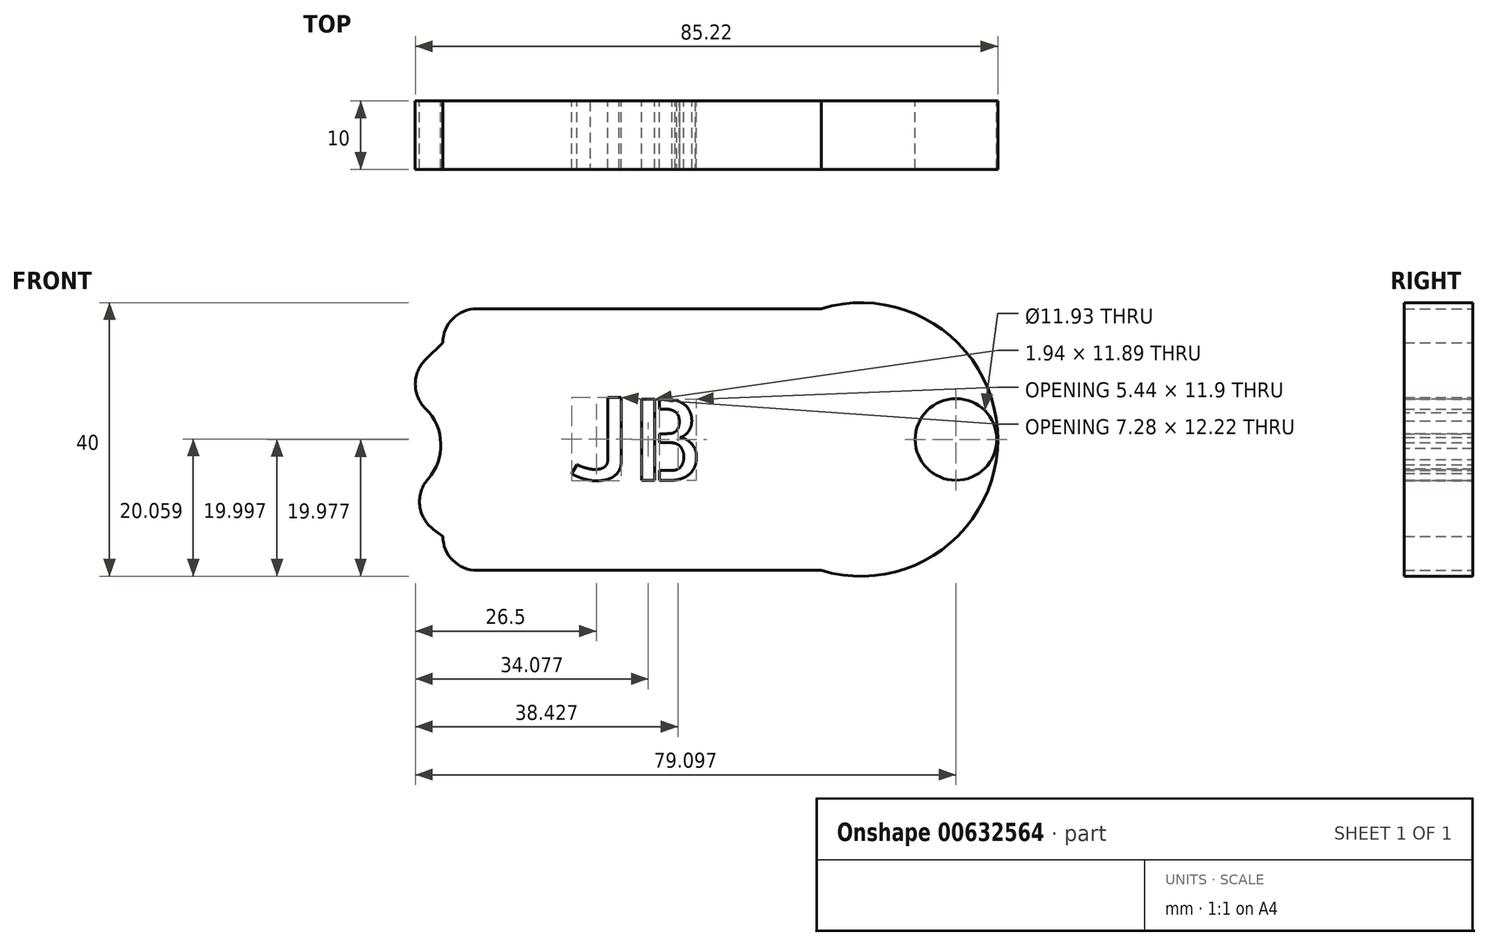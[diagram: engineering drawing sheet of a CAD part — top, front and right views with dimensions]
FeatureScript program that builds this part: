
annotation { "Feature Type Name" : "Feature", "Feature Type Description" : "" }
export const myFeature = defineFeature(function(context is Context, id is Id, definition is map)
    precondition{}
    {
        {
            var Q0;
            Q0=qCreatedBy(makeId("Front.planeOp"),FACE);
            var sketch = newSketch(context, id + "F0", { "sketchPlane" : qUnion([Q0])});
            skLineSegment(sketch, "E0.bottom", {"start": v(0, 0) * mm, "end": v(-50.38, 0) * mm});
            skLineSegment(sketch, "E0.top", {"start": v(0, 38.27) * mm, "end": v(-50.38, 38.27) * mm});
            skLineSegment(sketch, "E0.left", {"start": v(0, 0) * mm, "end": v(0, 38.27) * mm});
            skLineSegment(sketch, "E0.right", {"start": v(-55.38, 5) * mm, "end": v(-55.38, 33.27) * mm});
            skArc(sketch, "E1", {"start": v(0, 0) * mm, "mid": v(25.81, 19.14) * mm, "end": v(0, 38.27) * mm});
            skPoint(sketch, "E2.visualSharp", {"position": v(-55.38, 38.27) * mm});
            skArc(sketch, "E2.filletArc", {"start": v(-50.38, 38.27) * mm, "mid": v(-53.92, 36.8) * mm, "end": v(-55.38, 33.27) * mm});
            skPoint(sketch, "E3.visualSharp", {"position": v(-55.38, 0) * mm});
            skArc(sketch, "E3.filletArc", {"start": v(-55.38, 5) * mm, "mid": v(-53.92, 1.46) * mm, "end": v(-50.38, 0) * mm});
            skLineSegment(sketch, "E4", {"start": v(-55.38, 33.27) * mm, "end": v(-57.9, 30.8) * mm});
            skLineSegment(sketch, "E5", {"start": v(-55.38, 5) * mm, "end": v(-56.75, 6) * mm});
            skArc(sketch, "E6", {"start": v(-57.55, 13.35) * mm, "mid": v(-55.67, 18.58) * mm, "end": v(-57.92, 23.66) * mm});
            skLineSegment(sketch, "E7", {"start": v(-63.31, 10.8) * mm, "end": v(-63.31, 18.3) * mm});
            skText(sketch, "E8", { "text": "JB", "fontName": "AllertaStencil-Regular.ttf"});
            skPoint(sketch, "E9.visualSharp", {"position": v(-63.03, 25.8) * mm});
            skArc(sketch, "E9.filletArc", {"start": v(-57.9, 30.8) * mm, "mid": v(-59.41, 27.24) * mm, "end": v(-57.92, 23.66) * mm});
            skPoint(sketch, "E10.visualSharp", {"position": v(-63.31, 10.8) * mm});
            skArc(sketch, "E10.filletArc", {"start": v(-57.55, 13.35) * mm, "mid": v(-58.77, 9.5) * mm, "end": v(-56.75, 6) * mm});
            skCircle(sketch, "E11", {"center": v(19.69, 19.14) * mm, "radius": 5.96 * mm});
            const initialGuessF0  = {"E8": [-0.03697, 0.01317, 1, 0, 0.0119]};
            skSetInitialGuess(sketch, initialGuessF0);
            skSolve(sketch);
        }
        {
            var Q0;
            Q0 = qSketchRegion(id + "F0", true);
            extrude(context, id + "F1", {"entities" : qUnion([Q0]), "endBound" : BoundingType.SYMMETRIC, "depth" : 10 * mm, "offsetDistance" : 25 * mm});
        }
    });
